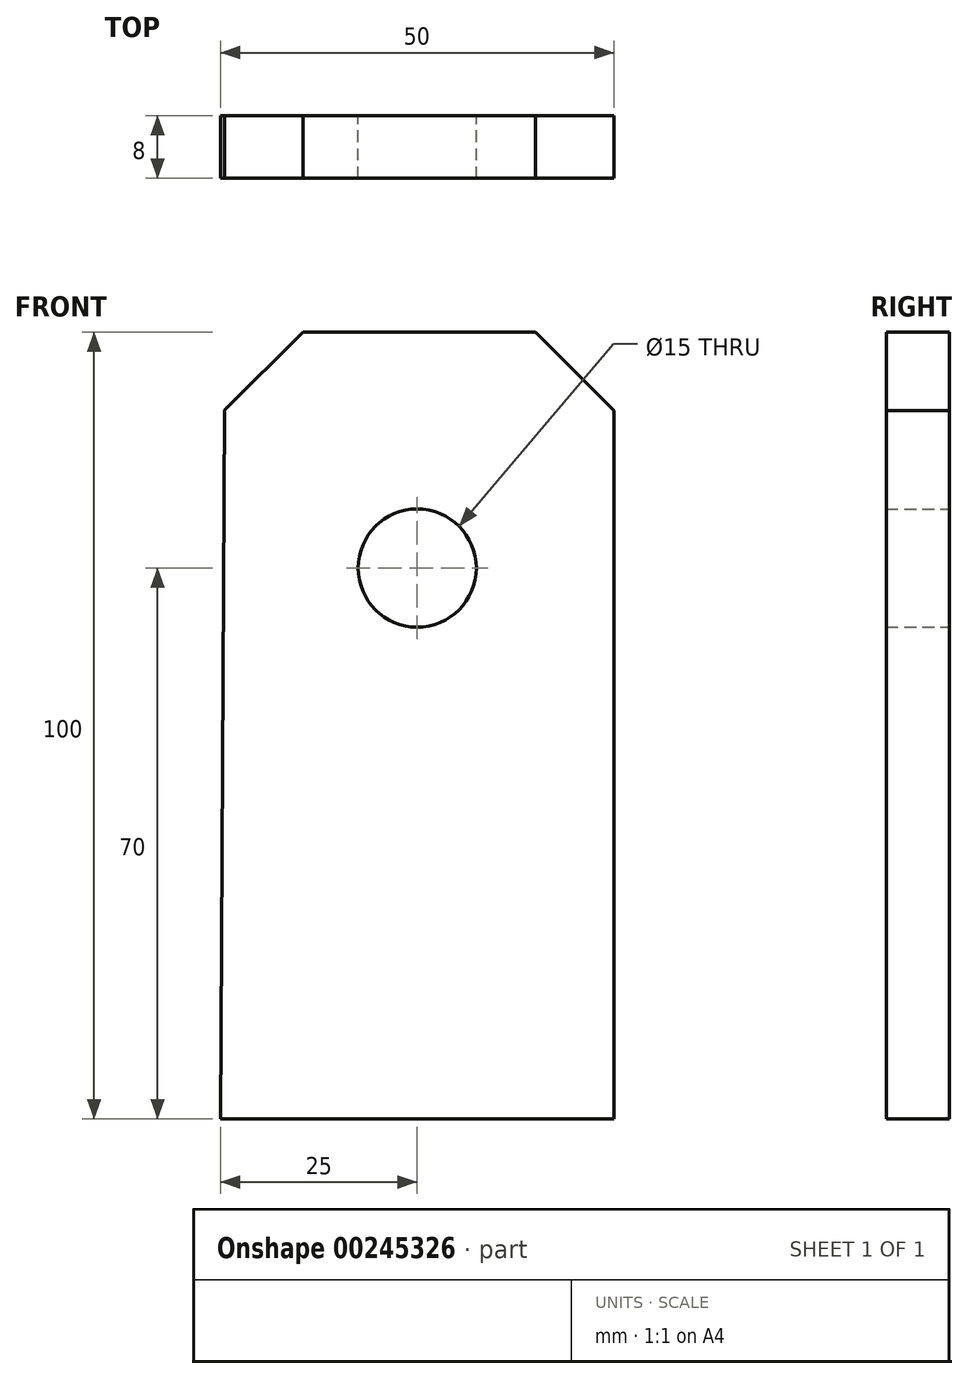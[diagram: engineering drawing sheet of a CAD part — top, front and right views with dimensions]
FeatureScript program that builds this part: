
annotation { "Feature Type Name" : "Feature", "Feature Type Description" : "" }
export const myFeature = defineFeature(function(context is Context, id is Id, definition is map)
    precondition{}
    {
        {
            var Q0;
            Q0=qCreatedBy(makeId("Front.planeOp"),FACE);
            var sketch = newSketch(context, id + "F0", { "sketchPlane" : qUnion([Q0])});
            skLineSegment(sketch, "E0.bottom", {"start": v(0, 0) * mm, "end": v(50, 0) * mm});
            skLineSegment(sketch, "E0.right", {"start": v(50, 0) * mm, "end": v(50, 100) * mm});
            skLineSegment(sketch, "E1.trimOffspring", {"start": v(0.57, 100) * mm, "end": v(50, 100) * mm});
            skCircle(sketch, "E2", {"center": v(25, 70) * mm, "radius": 7.5 * mm});
            skLineSegment(sketch, "E3", {"start": v(0.57, 100) * mm, "end": v(0, 0) * mm});
            skSolve(sketch);
        }
        {
            var Q0;
            Q0 = qSketchRegion(id + "F0", true);
            extrude(context, id + "F1", {"entities" : qUnion([Q0]), "depth" : 8 * mm});
        }
        {
            var Q0;
            Q0=makeQuery(id+"F1.opExtrude","SWEPT_EDGE",EDGE,{"disambiguationData":[OSD([sQuery(id+"F0.wireOp",EDGE,"E1.trimOffspring"),sQuery(id+"F0.wireOp",EDGE,"E3")])]});
            var Q1;
            Q1=makeQuery(id+"F1.opExtrude","SWEPT_EDGE",EDGE,{"disambiguationData":[OSD([sQuery(id+"F0.wireOp",EDGE,"E0.right"),sQuery(id+"F0.wireOp",EDGE,"E1.trimOffspring")])]});
            chamfer(context, id + "F2", {"entities" : qUnion([Q0, Q1]), "width" : 10 * mm, "tangentPropagation" : true});
        }
    });
